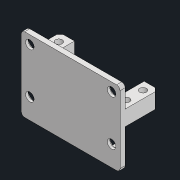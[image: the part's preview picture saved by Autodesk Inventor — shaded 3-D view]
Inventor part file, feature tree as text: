
AUTODESK INVENTOR PART (.ipt)
format: ipt  version: 2022.2 (Build 262287010, 287A)  size: 213,504 bytes
history: native  units: mm
features: reference x10, extrude x5, sketch x5, other x3, chamfer x2, mirror x1, fillet x1
ambient origin geometry x8: Origin, YZ Plane, XZ Plane, XY Plane, X Axis, Y Axis, Z Axis, Center Point
bodies: Solid1 (feature_tree)
feature tree (27):
  extrude  "Extrusion1"  TaperAngle=0.0deg  [1 undecoded]
  extrude  "Extrusion6"  Depth=2.0mm
  extrude  "Extrusion7"  Depth=9.0mm
  extrude  "Extrusion4"  Depth=2.0mm
  chamfer  "Chamfer1"  Distance=0.1mm
  chamfer  "Chamfer4"  Distance=0.1mm
  extrude  "Extrusion8"  TaperAngle=0.0deg  [1 undecoded]
  mirror  "Mirror1"
  fillet  "Fillet1"  [1 undecoded]
  sketch  "Sketch1"  dims[d1=3.0mm d2=0.0mm d40=0.0mm d41=0.0mm]
  sketch  "Sketch2"  dims[d42=1.5mm d43=2.0mm d44=45.0deg d54=2.0mm]
  sketch  "Sketch5"  dims[d66=9.0mm d67=0.5mm]
  reference  "Reference16"
  reference  "Reference17"
  reference  "Reference19"
  reference  "Reference20"
  reference  "Reference21"
  sketch  "Sketch7"  dims[d68=0.5mm d79=2.0mm]
  reference  "Reference27"
  reference  "Reference28"
  reference  "Reference29"
  sketch  "Sketch8"  dims[d82=0.1mm d83=0.1mm d84=0.1mm d86=0.0mm d88=0.0mm d89=5.0mm d90=5.0mm d91=5.0mm d93=2.0mm d94=2.0mm d95=45.0deg d96=10.0mm d97=0.0mm d99=4.0mm d17=0.5mm d18=0.872665mm d19=0.5mm d20=0.872665mm d85=0.5mm d87=0.5mm]
  reference  "Reference30"
  reference  "Reference31"
  parser-record x1  (decoder bookkeeping rows leaked as tree rows — omitted from the tree; the rows remain in map.json)
  other  "Assembly1.iam"
  other  "Servo_Motor_MG996R:1"
note: 3 required parameter values undecoded (feature->parameter linkage not recoverable at this tier; creation-order binding heuristic only, values carry confidence <= 0.55)
note: 1 file-system path scrubbed to <path> (originals preserved in map.json)
